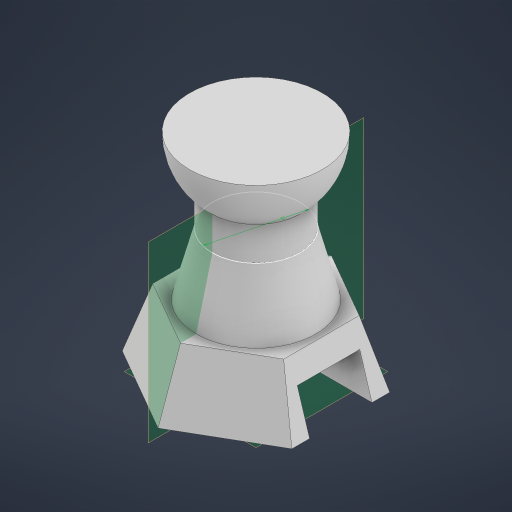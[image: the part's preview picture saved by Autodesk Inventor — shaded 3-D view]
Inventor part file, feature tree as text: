
AUTODESK INVENTOR PART (.ipt)
format: ipt  version: 2024.3 (Build 283343000, 343)  size: 256,000 bytes
history: native  units: mm
features: sketch x9, plane x3, loft x3, extrude x1, revolve x1, other x1
ambient origin geometry x8: Origin, YZ Plane, XZ Plane, XY Plane, X Axis, Y Axis, Z Axis, Center Point
bodies: Solid1 (feature_tree)
feature tree (18):
  extrude  "Extrusion1"  Depth=16.0mm TaperAngle=0.0deg
  sketch  "Sketch3"  dims[d4=42.0mm d5=30.0mm]
  plane  "Work Plane1"
  loft  "Loft1"
  sketch  "Sketch5"  dims[d12=30.0mm d17=0.0mm d18=90.0deg]
  plane  "Work Plane2"
  sketch  "Sketch6"  dims[d19=0.0mm d20=90.0deg d30=0.0mm d31=90.0deg]
  loft  "Loft3"
  loft  "Loft4"
  plane  "Work Plane4"
  revolve  "Revolution1"  Angle=90.0deg
  sketch  "Sketch2"  dims[d1=42.0mm d2=16.0mm d3=0.0mm]
  sketch  "Sketch4"  dims[d6=57.54mm d7=0.0mm d8=90.0deg d9=0.0mm d10=90.0deg]
  other  "Edges1"
  sketch  "Sketch8"  dims[d32=0.0mm d33=90.0deg]
  sketch  "Sketch9"  dims[d38=90.0deg]
  sketch  "Sketch10"  dims[d40=15.0mm]
  sketch  "Sketch12"  dims[d41=20.0mm d42=30.0mm]
